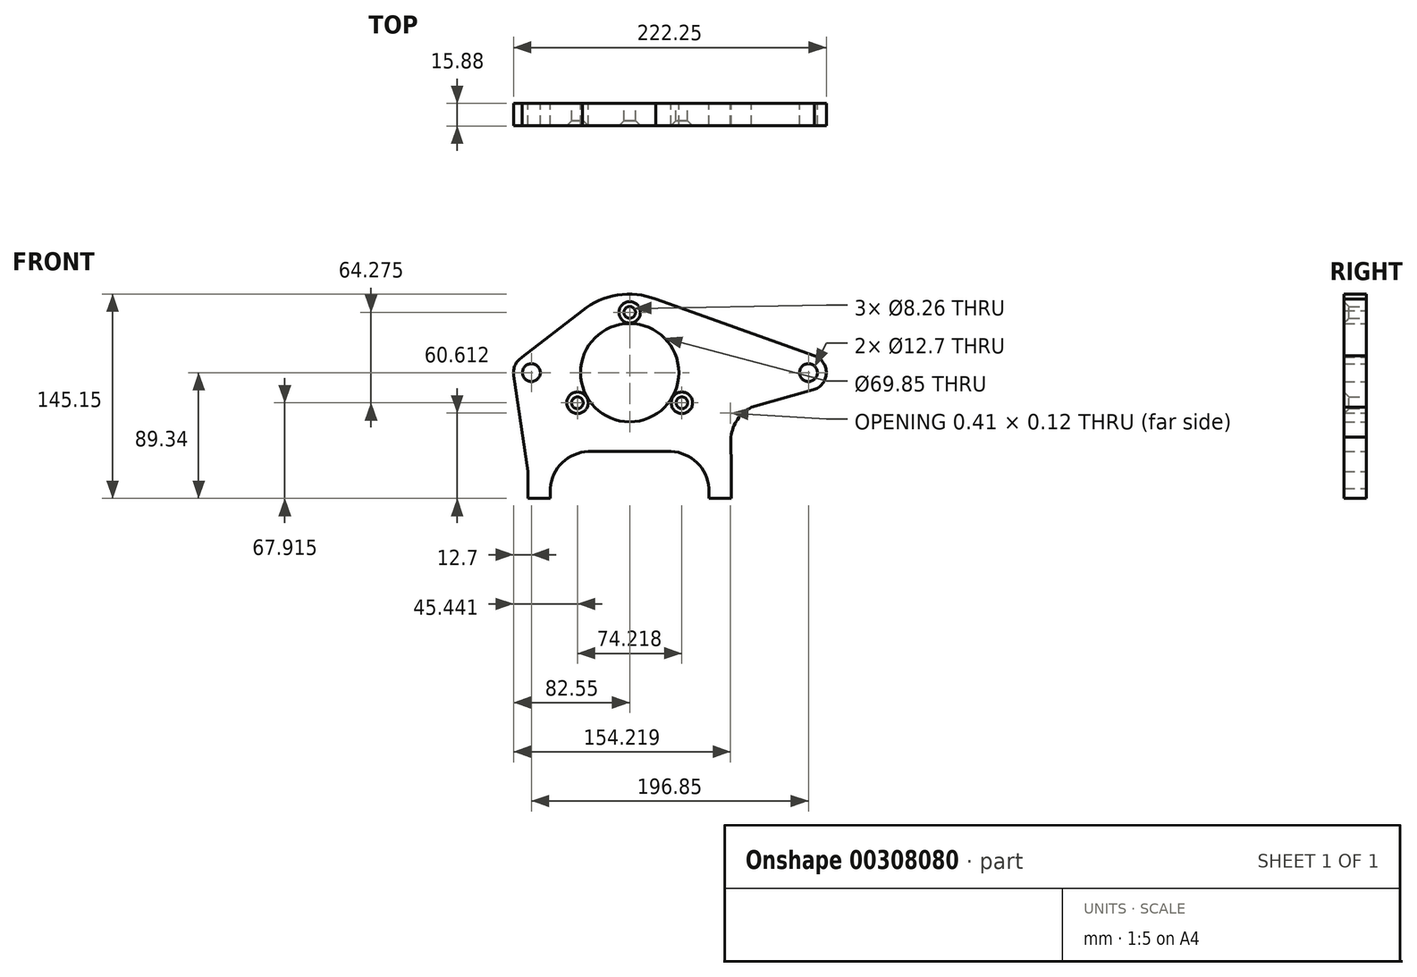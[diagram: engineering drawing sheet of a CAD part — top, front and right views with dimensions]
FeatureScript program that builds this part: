
annotation { "Feature Type Name" : "Feature", "Feature Type Description" : "" }
export const myFeature = defineFeature(function(context is Context, id is Id, definition is map)
    precondition{}
    {
        {
            var Q0;
            Q0=qCreatedBy(makeId("Front.planeOp"),FACE);
            var sketch = newSketch(context, id + "F0", { "sketchPlane" : qUnion([Q0])});
            skArc(sketch, "E0", {"start": v(-32.34, -13.18) * mm, "mid": v(0, -34.93) * mm, "end": v(32.34, -13.18) * mm});
            skCircle(sketch, "E1", {"center": v(-37.1, -21.42) * mm, "radius": 4.13 * mm});
            skCircle(sketch, "E2.MirrorC", {"center": v(37.1, -21.42) * mm, "radius": 4.13 * mm});
            skPoint(sketch, "E3.orphan", {"position": v(0, -34.93) * mm});
            skLineSegment(sketch, "E4.0", {"start": v(-29.37, -56) * mm, "end": v(29.37, -56) * mm});
            skLineSegment(sketch, "E5.0", {"start": v(-72.23, -89.34) * mm, "end": v(-56.36, -89.34) * mm});
            skLineSegment(sketch, "E6", {"start": v(0, -34.93) * mm, "end": v(0, -56) * mm});
            skLineSegment(sketch, "E7.0", {"start": v(72.23, -70.3) * mm, "end": v(72.23, -89.34) * mm});
            skLineSegment(sketch, "E8.0", {"start": v(-72.23, -70.3) * mm, "end": v(-72.23, -89.34) * mm});
            skLineSegment(sketch, "E9.0", {"start": v(56.36, -82.25) * mm, "end": v(56.36, -89.34) * mm});
            skLineSegment(sketch, "E10.0", {"start": v(-56.36, -82.25) * mm, "end": v(-56.36, -89.34) * mm});
            skArc(sketch, "E11", {"start": v(56.36, -82.25) * mm, "mid": v(47.02, -63.17) * mm, "end": v(27.03, -56) * mm});
            skPoint(sketch, "E11.first.point", {"position": v(56.36, -86.17) * mm});
            skPoint(sketch, "E11.second.point", {"position": v(27.03, -56) * mm});
            skLineSegment(sketch, "E12.trimOffspring", {"start": v(55.95, -89.34) * mm, "end": v(72.23, -89.34) * mm});
            skArc(sketch, "E13.MirrorCS", {"start": v(-56.36, -86.17) * mm, "mid": v(-48.44, -64.53) * mm, "end": v(-27.03, -56) * mm});
            skPoint(sketch, "E14.orphan", {"position": v(27.58, -21.42) * mm});
            skPoint(sketch, "E15.orphan", {"position": v(-27.58, -21.42) * mm});
            skLineSegment(sketch, "E16", {"start": v(0, -34.93) * mm, "end": v(0, 66.57) * mm, "construction": true});
            skCircle(sketch, "E17", {"center": v(0, 42.85) * mm, "radius": 4.13 * mm});
            skCircle(sketch, "E18", {"center": v(0, 0) * mm, "radius": 34.93 * mm});
            skLineSegment(sketch, "E19", {"start": v(-126.46, 0) * mm, "end": v(146.74, 0) * mm, "construction": true});
            skLineSegment(sketch, "E20.0", {"start": v(127, -34.93) * mm, "end": v(127, 66.57) * mm});
            skArc(sketch, "E21", {"start": v(-76.26, 10.97) * mm, "mid": v(-81.3, 5.5) * mm, "end": v(-82.41, -1.87) * mm});
            skArc(sketch, "E22", {"start": v(130.43, -12.23) * mm, "mid": v(139.7, -0.37) * mm, "end": v(131.14, 12) * mm});
            skLineSegment(sketch, "E23", {"start": v(-72.23, -70.3) * mm, "end": v(-82.41, -1.87) * mm});
            skLineSegment(sketch, "E24", {"start": v(-76.26, 10.97) * mm, "end": v(-33.59, 44.02) * mm});
            skLineSegment(sketch, "E25", {"start": v(131.14, 12) * mm, "end": v(18.6, 52.19) * mm});
            skLineSegment(sketch, "E26", {"start": v(130.43, -12.23) * mm, "end": v(86.61, -24.53) * mm});
            skCircle(sketch, "E27", {"center": v(-69.85, 0) * mm, "radius": 6.35 * mm});
            skCircle(sketch, "E28", {"center": v(127, 0) * mm, "radius": 6.35 * mm});
            skArc(sketch, "E29.trimOffspring", {"start": v(18.6, 52.19) * mm, "mid": v(-8.6, 55.19) * mm, "end": v(-33.59, 44.02) * mm});
            skArc(sketch, "E30", {"start": v(71.88, -28.67) * mm, "mid": v(71.67, -28.73) * mm, "end": v(71.46, -28.79) * mm});
            skPoint(sketch, "E30.second.point", {"position": v(71.88, -28.67) * mm});
            skLineSegment(sketch, "E31", {"start": v(72.23, -70.3) * mm, "end": v(72.02, -45.68) * mm});
            skArc(sketch, "E32", {"start": v(96.66, -21.71) * mm, "mid": v(77.93, -31.52) * mm, "end": v(72.07, -51.82) * mm});
            skPoint(sketch, "E32.first.point", {"position": v(72.02, -45.68) * mm});
            skPoint(sketch, "E32.second.point", {"position": v(86.61, -24.53) * mm});
            skPoint(sketch, "E32.third.point", {"position": v(81.5, -27.9) * mm});
            skLineSegment(sketch, "E33.trimOffspring", {"start": v(71.88, -28.67) * mm, "end": v(71.46, -28.79) * mm});
            skSolve(sketch);
        }
        {
            var Q0;
            Q0 = qSketchRegion(id + "F0", true);
            extrude(context, id + "F1", {"entities" : qUnion([Q0]), "depth" : 15.88 * mm, "offsetDistance" : 25.4 * mm});
        }
        {
            var Q0;
            Q0=makeQuery(id+"F1.opExtrude","CAP_FACE",FACE,{"disambiguationData":[OSD([sQuery(id+"F0.wireOp",EDGE,"E0"),sQuery(id+"F0.wireOp",EDGE,"E1"),sQuery(id+"F0.wireOp",EDGE,"E2.MirrorC"),sQuery(id+"F0.wireOp",EDGE,"E4.0"),sQuery(id+"F0.wireOp",EDGE,"E5.0"),sQuery(id+"F0.wireOp",EDGE,"E7.0"),sQuery(id+"F0.wireOp",EDGE,"E8.0"),sQuery(id+"F0.wireOp",EDGE,"E9.0"),sQuery(id+"F0.wireOp",EDGE,"E10.0"),sQuery(id+"F0.wireOp",EDGE,"E11"),sQuery(id+"F0.wireOp",EDGE,"E12.trimOffspring"),sQuery(id+"F0.wireOp",EDGE,"E13.MirrorCS"),sQuery(id+"F0.wireOp",EDGE,"E17"),sQuery(id+"F0.wireOp",EDGE,"E18"),sQuery(id+"F0.wireOp",EDGE,"E21"),sQuery(id+"F0.wireOp",EDGE,"E22"),sQuery(id+"F0.wireOp",EDGE,"E23"),sQuery(id+"F0.wireOp",EDGE,"E24"),sQuery(id+"F0.wireOp",EDGE,"E25"),sQuery(id+"F0.wireOp",EDGE,"E26"),sQuery(id+"F0.wireOp",EDGE,"E27"),sQuery(id+"F0.wireOp",EDGE,"E28"),sQuery(id+"F0.wireOp",EDGE,"E29.trimOffspring"),sQuery(id+"F0.wireOp",EDGE,"E30"),sQuery(id+"F0.wireOp",EDGE,"E31"),sQuery(id+"F0.wireOp",EDGE,"E32"),sQuery(id+"F0.wireOp",EDGE,"E33.trimOffspring")])],"isStart":false});
            var sketch = newSketch(context, id + "F2", { "sketchPlane" : qUnion([Q0])});
            skCircle(sketch, "E34.0", {"center": v(-37.1, -21.42) * mm, "radius": 4.13 * mm});
            skCircle(sketch, "E34.1", {"center": v(37.1, -21.42) * mm, "radius": 4.13 * mm});
            skCircle(sketch, "E34.2", {"center": v(0, 42.85) * mm, "radius": 4.13 * mm});
            skSolve(sketch);
        }
        {
            var Q0;
            Q0=sQuery(id+"F2.wireOp",VERTEX,"E34.0.center");
            var Q1;
            Q1=sQuery(id+"F2.wireOp",VERTEX,"E34.2.center");
            var Q2;
            Q2=sQuery(id+"F2.wireOp",VERTEX,"E34.1.center");
            var Q3;
            Q3=makeQuery(id+"F1.opExtrude","SWEPT_BODY",BODY,{"disambiguationData":[OSD([sQuery(id+"F0.wireOp",EDGE,"E0"),sQuery(id+"F0.wireOp",EDGE,"E1"),sQuery(id+"F0.wireOp",EDGE,"E2.MirrorC"),sQuery(id+"F0.wireOp",EDGE,"E4.0"),sQuery(id+"F0.wireOp",EDGE,"E5.0"),sQuery(id+"F0.wireOp",EDGE,"E7.0"),sQuery(id+"F0.wireOp",EDGE,"E8.0"),sQuery(id+"F0.wireOp",EDGE,"E9.0"),sQuery(id+"F0.wireOp",EDGE,"E10.0"),sQuery(id+"F0.wireOp",EDGE,"E11"),sQuery(id+"F0.wireOp",EDGE,"E12.trimOffspring"),sQuery(id+"F0.wireOp",EDGE,"E13.MirrorCS"),sQuery(id+"F0.wireOp",EDGE,"E17"),sQuery(id+"F0.wireOp",EDGE,"E18"),sQuery(id+"F0.wireOp",EDGE,"E21"),sQuery(id+"F0.wireOp",EDGE,"E22"),sQuery(id+"F0.wireOp",EDGE,"E23"),sQuery(id+"F0.wireOp",EDGE,"E24"),sQuery(id+"F0.wireOp",EDGE,"E25"),sQuery(id+"F0.wireOp",EDGE,"E26"),sQuery(id+"F0.wireOp",EDGE,"E27"),sQuery(id+"F0.wireOp",EDGE,"E28"),sQuery(id+"F0.wireOp",EDGE,"E29.trimOffspring"),sQuery(id+"F0.wireOp",EDGE,"E30"),sQuery(id+"F0.wireOp",EDGE,"E31"),sQuery(id+"F0.wireOp",EDGE,"E32"),sQuery(id+"F0.wireOp",EDGE,"E33.trimOffspring")])]});
            hole(context, id + "F3", {"style" : HoleStyle.C_SINK, "endStyle" : HoleEndStyle.THROUGH, "holeDiameter" : 8.25 * mm, "cSinkDiameter" : 15.24 * mm, "cSinkAngle" : 90 * degree, "majorDiameter" : 6.35 * mm, "isTappedThrough" : true, "tappedDepth" : 12.7 * mm, "tapClearance" : 3, "startFromSketch" : true, "locations" : qUnion([Q0, Q1, Q2]), "scope" : qUnion([Q3])});
        }
    });
